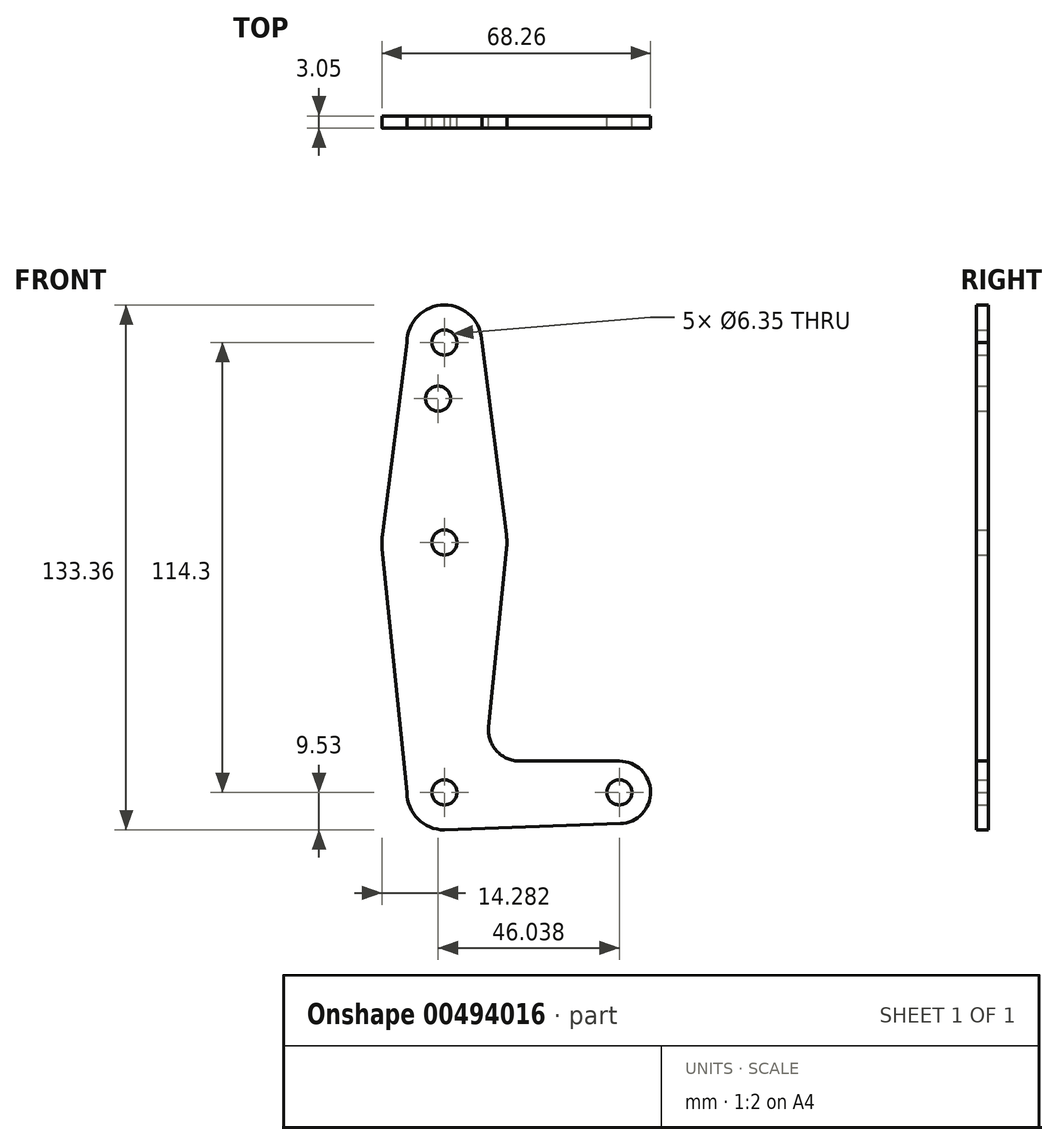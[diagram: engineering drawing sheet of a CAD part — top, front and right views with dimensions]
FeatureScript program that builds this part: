
annotation { "Feature Type Name" : "Feature", "Feature Type Description" : "" }
export const myFeature = defineFeature(function(context is Context, id is Id, definition is map)
    precondition{}
    {
        {
            var Q0;
            Q0=qCreatedBy(makeId("Front.planeOp"),FACE);
            var sketch = newSketch(context, id + "F0", { "sketchPlane" : qUnion([Q0])});
            skLineSegment(sketch, "E0", {"start": v(0, 0) * mm, "end": v(0, 114.3) * mm, "construction": true});
            skCircle(sketch, "E1", {"center": v(0, 114.3) * mm, "radius": 9.53 * mm});
            skCircle(sketch, "E2", {"center": v(0, 0) * mm, "radius": 9.53 * mm});
            skCircle(sketch, "E3", {"center": v(0, 63.5) * mm, "radius": 15.88 * mm});
            skLineSegment(sketch, "E4", {"start": v(0, 0) * mm, "end": v(44.45, 0) * mm, "construction": true});
            skCircle(sketch, "E5", {"center": v(44.45, 0) * mm, "radius": 7.94 * mm});
            skLineSegment(sketch, "E6", {"start": v(-9.53, 114.3) * mm, "end": v(-15.75, 65.5) * mm});
            skLineSegment(sketch, "E7", {"start": v(9.53, 114.3) * mm, "end": v(15.75, 65.5) * mm});
            skLineSegment(sketch, "E8", {"start": v(-15.8, 61.9) * mm, "end": v(-9.52, 0) * mm});
            skLineSegment(sketch, "E9", {"start": v(19.16, 7.94) * mm, "end": v(44.45, 7.94) * mm});
            skLineSegment(sketch, "E10", {"start": v(0, -9.53) * mm, "end": v(44.73, -7.93) * mm});
            skLineSegment(sketch, "E11", {"start": v(15.8, 61.9) * mm, "end": v(11.25, 16.68) * mm});
            skCircle(sketch, "E12", {"center": v(0, 114.3) * mm, "radius": 3.18 * mm});
            skCircle(sketch, "E13", {"center": v(-1.59, 100.03) * mm, "radius": 3.18 * mm});
            skCircle(sketch, "E14", {"center": v(0, 63.5) * mm, "radius": 3.18 * mm});
            skCircle(sketch, "E15", {"center": v(0, 0) * mm, "radius": 3.18 * mm});
            skCircle(sketch, "E16", {"center": v(44.45, 0) * mm, "radius": 3.18 * mm});
            skPoint(sketch, "E17.newPointA", {"position": v(9.57, 0) * mm});
            skArc(sketch, "E17.filletArc", {"start": v(11.25, 16.68) * mm, "mid": v(13.26, 10.55) * mm, "end": v(19.16, 7.94) * mm});
            skSolve(sketch);
        }
        {
            var Q0;
            Q0=makeQuery(id+"F0.imprint","IMPRINT",FACE,{"disambiguationData":[TD([[makeQuery(id+"F0.imprint","IMPRINT",EDGE,{"derivedFrom":sQuery(id+"F0.wireOp",EDGE,"E12")}),-1.0]])]});
            var Q1;
            {var subQ1=sQuery(id+"F0.wireOp",EDGE,"E6");Q1=makeQuery(id+"F0.imprint","IMPRINT",FACE,{"disambiguationData":[TD([[makeQuery(id+"F0.imprint","IMPRINT",EDGE,{"derivedFrom":subQ1}),1.0]])]});}
            var Q2;
            Q2=makeQuery(id+"F0.imprint","IMPRINT",FACE,{"disambiguationData":[TD([[makeQuery(id+"F0.imprint","IMPRINT",EDGE,{"derivedFrom":sQuery(id+"F0.wireOp",EDGE,"E14")}),-1.0]])]});
            var Q3;
            {var subQ0=sQuery(id+"F0.wireOp",EDGE,"E8");Q3=makeQuery(id+"F0.imprint","IMPRINT",FACE,{"disambiguationData":[TD([[makeQuery(id+"F0.imprint","IMPRINT",EDGE,{"derivedFrom":subQ0}),1.0]])]});}
            var Q4;
            Q4=makeQuery(id+"F0.imprint","IMPRINT",FACE,{"disambiguationData":[TD([[makeQuery(id+"F0.imprint","IMPRINT",EDGE,{"derivedFrom":sQuery(id+"F0.wireOp",EDGE,"E15")}),-1.0]])]});
            var Q5;
            Q5=makeQuery(id+"F0.imprint","IMPRINT",FACE,{"disambiguationData":[TD([[makeQuery(id+"F0.imprint","IMPRINT",EDGE,{"derivedFrom":sQuery(id+"F0.wireOp",EDGE,"E16")}),-1.0]])]});
            extrude(context, id + "F1", {"entities" : qUnion([Q0, Q1, Q2, Q3, Q4, Q5]), "depth" : 3.05 * mm});
        }
    });
